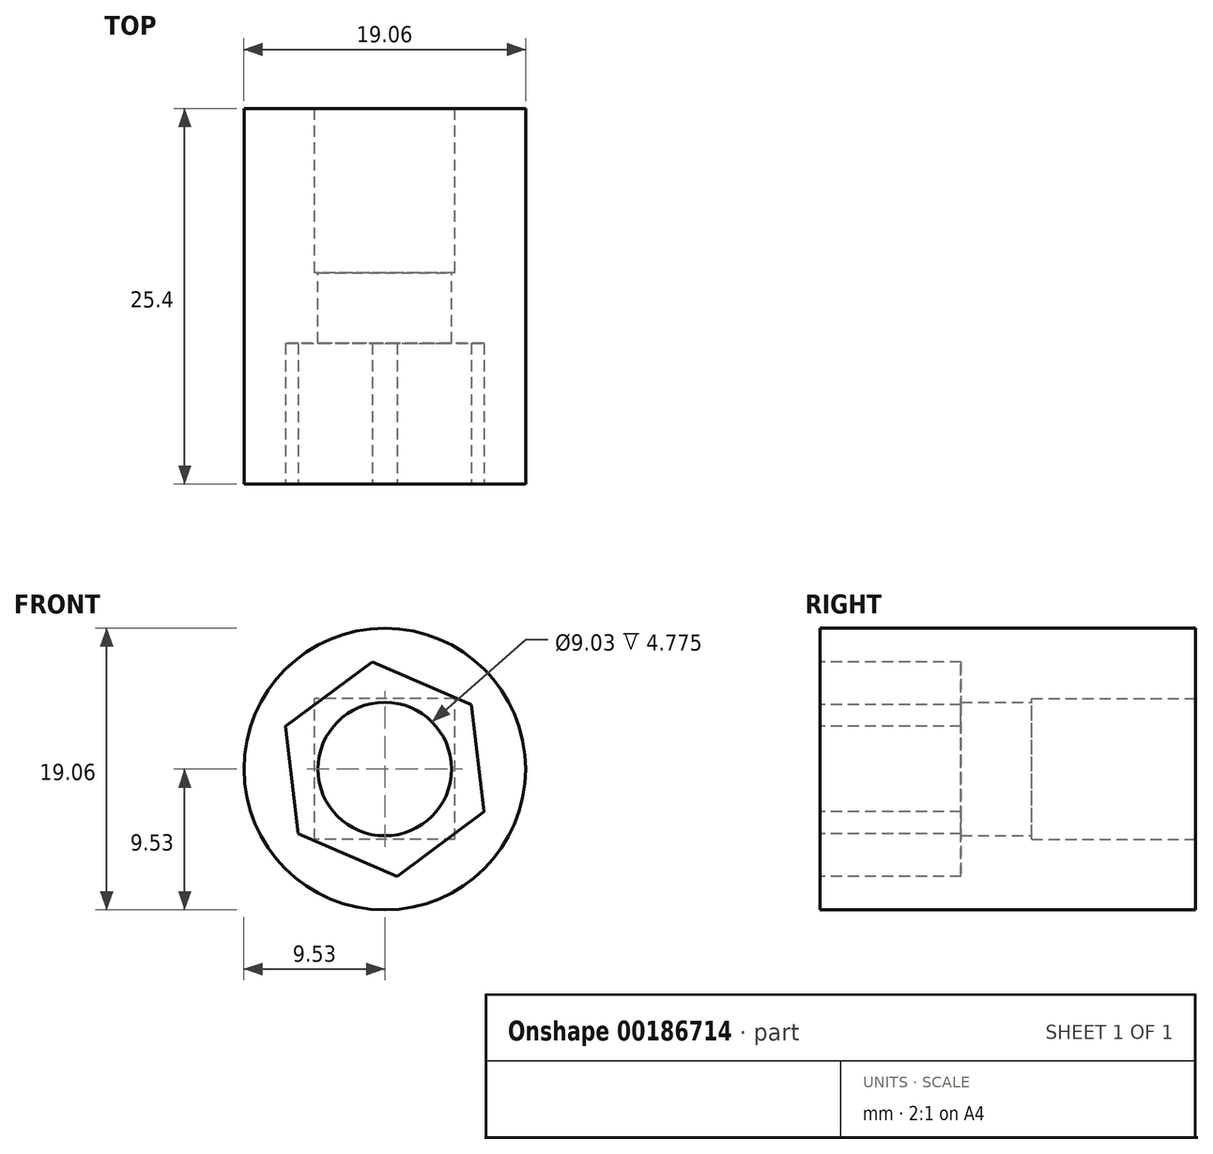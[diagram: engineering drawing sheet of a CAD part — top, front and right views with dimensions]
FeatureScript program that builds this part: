
annotation { "Feature Type Name" : "Feature", "Feature Type Description" : "" }
export const myFeature = defineFeature(function(context is Context, id is Id, definition is map)
    precondition{}
    {
        {
            var Q0;
            Q0=qCreatedBy(makeId("Front.planeOp"),FACE);
            var sketch = newSketch(context, id + "F0", { "sketchPlane" : qUnion([Q0])});
            skCircle(sketch, "E0", {"center": v(0, 0) * mm, "radius": 9.53 * mm});
            skSolve(sketch);
        }
        {
            var Q0;
            Q0 = qSketchRegion(id + "F0", true);
            extrude(context, id + "F1", {"entities" : qUnion([Q0]), "depth" : 25.4 * mm});
        }
        {
            var Q0;
            Q0=qCreatedBy(makeId("Front.planeOp"),FACE);
            var sketch = newSketch(context, id + "F2", { "sketchPlane" : qUnion([Q0])});
            skLineSegment(sketch, "E1.bottom", {"start": v(4.76, -4.76) * mm, "end": v(-4.76, -4.76) * mm});
            skLineSegment(sketch, "E1.top", {"start": v(4.76, 4.76) * mm, "end": v(-4.76, 4.76) * mm});
            skLineSegment(sketch, "E1.left", {"start": v(4.76, -4.76) * mm, "end": v(4.76, 4.76) * mm});
            skLineSegment(sketch, "E1.right", {"start": v(-4.76, -4.76) * mm, "end": v(-4.76, 4.76) * mm});
            skPoint(sketch, "E1.middle", {"position": v(0, 0) * mm});
            skCircle(sketch, "E2", {"center": v(0, 0) * mm, "radius": 4.52 * mm});
            skSolve(sketch);
        }
        {
            var Q0;
            Q0=makeQuery(id+"F2.imprint","IMPRINT",FACE,{"disambiguationData":[TD([[makeQuery(id+"F2.imprint","IMPRINT",EDGE,{"derivedFrom":sQuery(id+"F2.wireOp",EDGE,"E2")}),1.0]])]});
            extrude(context, id + "F3", {"entities" : qUnion([Q0]), "operationType" : NewBodyOperationType.REMOVE, "endBound" : BoundingType.THROUGH_ALL, "depth" : 25.4 * mm});
        }
        {
            var Q0;
            Q0 = qSketchRegion(id + "F2", true);
            extrude(context, id + "F4", {"entities" : qUnion([Q0]), "operationType" : NewBodyOperationType.REMOVE, "depth" : 11.1 * mm});
        }
        {
            var Q0;
            Q0=makeQuery(id+"F1.opExtrude","CAP_FACE",FACE,{"disambiguationData":[OSD([sQuery(id+"F0.wireOp",EDGE,"E0")])],"isStart":false});
            var sketch = newSketch(context, id + "F5", { "sketchPlane" : qUnion([Q0])});
            skCircle(sketch, "E3.cCircle", {"center": v(0, 0) * mm, "radius": 6.32 * mm, "construction": true});
            skLineSegment(sketch, "E3.0", {"start": v(-6.7, 2.88) * mm, "end": v(-0.86, 7.25) * mm});
            skLineSegment(sketch, "E3.1", {"start": v(-0.86, 7.25) * mm, "end": v(5.85, 4.37) * mm});
            skLineSegment(sketch, "E3.2", {"start": v(5.85, 4.37) * mm, "end": v(6.7, -2.88) * mm});
            skLineSegment(sketch, "E3.3", {"start": v(6.7, -2.88) * mm, "end": v(0.86, -7.25) * mm});
            skLineSegment(sketch, "E3.4", {"start": v(0.86, -7.25) * mm, "end": v(-5.85, -4.37) * mm});
            skLineSegment(sketch, "E3.5", {"start": v(-5.85, -4.37) * mm, "end": v(-6.7, 2.88) * mm});
            skPoint(sketch, "E3.0.midPoint", {"position": v(-3.78, 5.07) * mm});
            skSolve(sketch);
        }
        {
            var Q0;
            Q0=makeQuery(id+"F5.imprint","IMPRINT",FACE,{"disambiguationData":[TD([[makeQuery(id+"F5.imprint","IMPRINT",EDGE,{"derivedFrom":makeQuery(id+"F3.boolean.opBoolean","INTERSECT",EDGE,{"derivedFrom":[makeQuery(id+"F1.opExtrude","CAP_FACE",FACE,{"disambiguationData":[OSD([sQuery(id+"F0.wireOp",EDGE,"E0")])],"isStart":false}),makeQuery(id+"F3.opExtrude","SWEPT_FACE",FACE,{"disambiguationData":[OSD([sQuery(id+"F2.wireOp",EDGE,"E2")])]})]})}),-1.0]])]});
            var Q1;
            Q1=makeQuery(id+"F5.imprint","IMPRINT",FACE,{"disambiguationData":[TD([[makeQuery(id+"F5.imprint","IMPRINT",EDGE,{"derivedFrom":sQuery(id+"F5.wireOp",EDGE,"E3.0")}),-1.0]])]});
            extrude(context, id + "F6", {"entities" : qUnion([Q0, Q1]), "operationType" : NewBodyOperationType.REMOVE, "oppositeDirection" : true, "depth" : 9.52 * mm});
        }
    });
